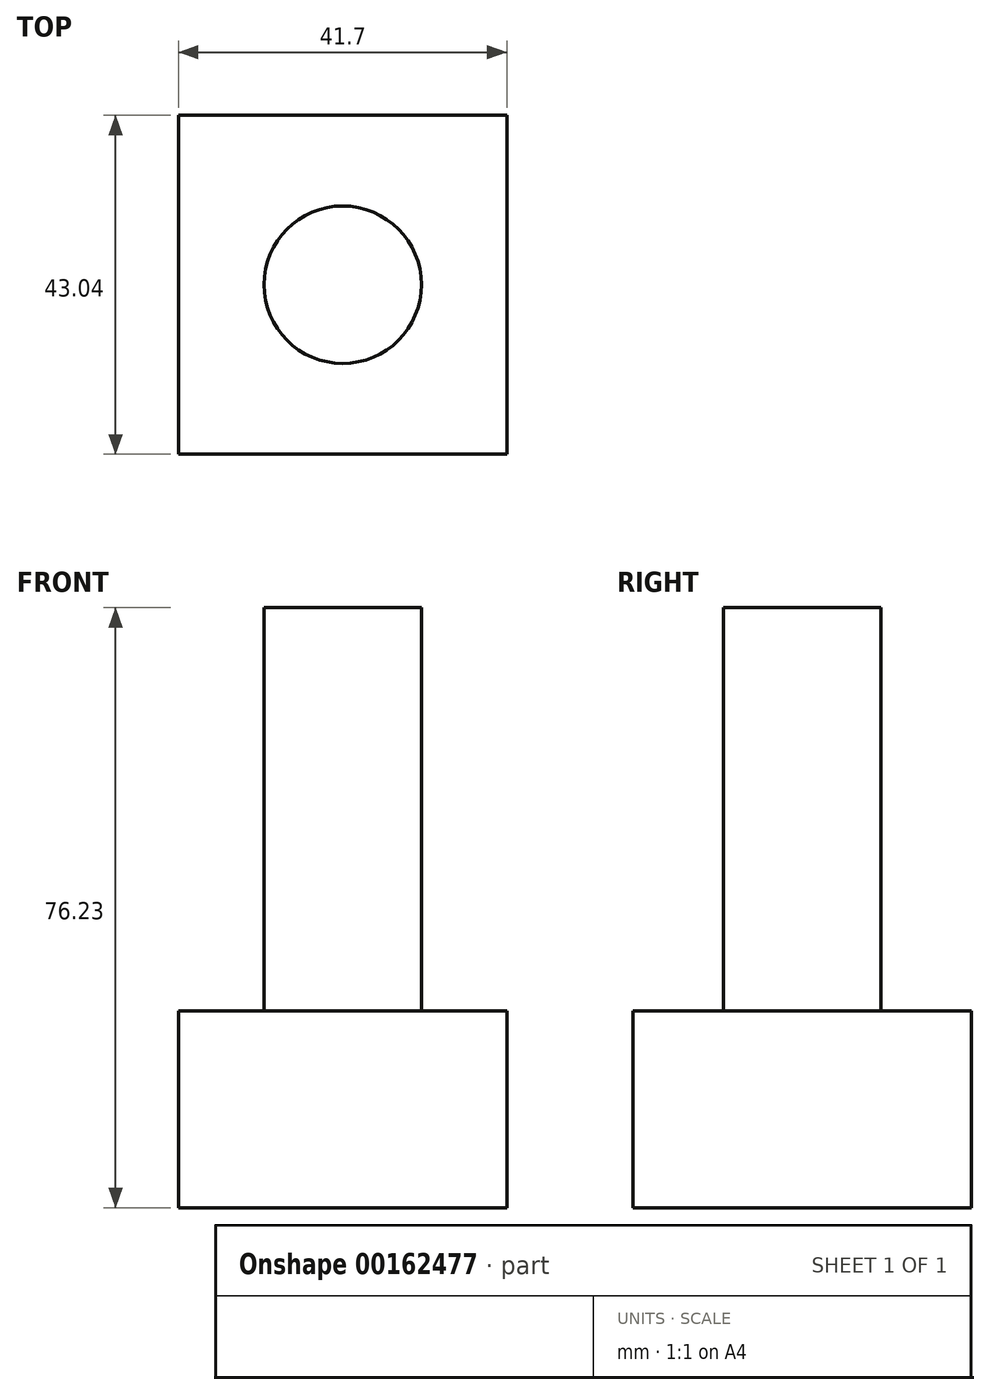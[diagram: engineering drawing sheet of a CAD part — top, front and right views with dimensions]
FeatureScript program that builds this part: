
annotation { "Feature Type Name" : "Feature", "Feature Type Description" : "" }
export const myFeature = defineFeature(function(context is Context, id is Id, definition is map)
    precondition{}
    {
        {
            var Q0;
            Q0=qCreatedBy(makeId("Top.planeOp"),FACE);
            var sketch = newSketch(context, id + "F0", { "sketchPlane" : qUnion([Q0])});
            skCircle(sketch, "E0", {"center": v(0, 0) * mm, "radius": 10 * mm});
            skSolve(sketch);
        }
        {
            var Q0;
            Q0 = qSketchRegion(id + "F0", true);
            extrude(context, id + "F1", {"entities" : qUnion([Q0]), "depth" : 76.23 * mm});
        }
        {
            var Q0;
            Q0=makeQuery(id+"F0.imprint","IMPRINT",FACE,{"disambiguationData":[TD([[makeQuery(id+"F0.imprint","IMPRINT",EDGE,{"derivedFrom":sQuery(id+"F0.wireOp",EDGE,"E0")}),1.0]])]});
            var sketch = newSketch(context, id + "F2", { "sketchPlane" : qUnion([Q0])});
            skLineSegment(sketch, "E1.bottom", {"start": v(20.85, 21.52) * mm, "end": v(-20.85, 21.52) * mm});
            skLineSegment(sketch, "E1.top", {"start": v(20.85, -21.52) * mm, "end": v(-20.85, -21.52) * mm});
            skLineSegment(sketch, "E1.left", {"start": v(20.85, 21.52) * mm, "end": v(20.85, -21.52) * mm});
            skLineSegment(sketch, "E1.right", {"start": v(-20.85, 21.52) * mm, "end": v(-20.85, -21.52) * mm});
            skPoint(sketch, "E1.middle", {"position": v(0, 0) * mm});
            skSolve(sketch);
        }
        {
            var Q0;
            Q0=makeQuery(id+"F2.imprint","IMPRINT",FACE,{"disambiguationData":[TD([[makeQuery(id+"F2.imprint","IMPRINT",EDGE,{"derivedFrom":sQuery(id+"F2.wireOp",EDGE,"E1.bottom")}),1.0]])]});
            extrude(context, id + "F3", {"entities" : qUnion([Q0]), "operationType" : NewBodyOperationType.ADD, "depth" : 25 * mm});
        }
    });
